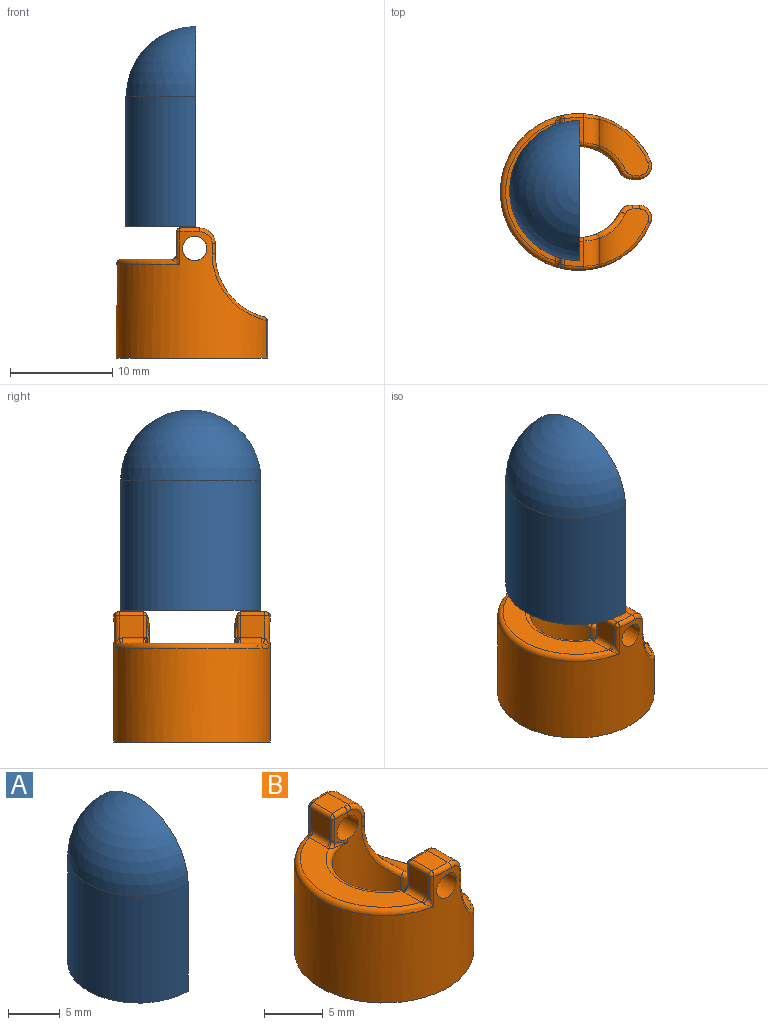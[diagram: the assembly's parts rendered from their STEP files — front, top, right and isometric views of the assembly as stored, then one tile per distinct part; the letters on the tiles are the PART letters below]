
ASSEMBLY  parts=2 mates=1
PART A: 6 faces, bbox 6.8x13.7x19.5 mm
  f0: cylinder r=6.85mm len=13.69mm, axis (0,0,1), area 273.1mm2, adj f1,f4,f5
  f1: plane 13.69x6.85mm, normal (0,0,-1), area 42.6mm2, adj f0,f2,f5
  f2: cylinder r=4.45mm len=12.7mm, axis (0,0,1), area 177.3mm2, adj f1,f3,f5
  f3: sphere r=4.45mm, area 62.1mm2, adj f2,f5
  f4: sphere r=6.85mm, area 147.2mm2, adj f0,f5
  f5: plane 19.55x13.69mm, normal (1,0,0), area 103.5mm2, adj f0,f1,f2,f3,f4
PART B: 72 faces, bbox 15.6x16.2x12.7 mm
  f0: cylinder r=7.64mm len=15.29mm, axis (0,0,-1), area 334.1mm2, adj f4,f5,f7,f9,f17,f19,f27,f29
  f1: cylinder r=4.45mm len=12.32mm, axis (0,0,-1), area 202.2mm2, adj f4,f5,f6,f9,f18,f20,f22,f24
  f2: plane 2.46x1.87mm, normal (0,0,1), area 4.5mm2, adj f7,f13,f28,f57,f59
  f3: plane 2.46x1.87mm, normal (0,0,1), area 4.5mm2, adj f6,f14,f33,f52,f54
  f4: cylinder r=1.2mm len=3.37mm, axis (0,1,0), area 24.1mm2, adj f0,f1,f44
  f5: cylinder r=1.2mm len=3.37mm, axis (0,1,0), area 24.1mm2, adj f0,f1,f43
  f6: torus R=4.83mm, axis (0,0,1), area 0.3mm2, adj f1,f3,f26,f54
  f7: torus R=7.26mm, axis (0,0,1), area 1.2mm2, adj f0,f2,f35,f56
  f8: cylinder r=6.35mm len=6.16mm, axis (0,1,0), area 23.6mm2, adj f11,f21,f22,f23,f25,f27
  f9: plane 15.29x14.76mm, normal (0,0,-1), area 111.7mm2, adj f0,f1,f15,f16,f17,f18,f19,f20
  f10: plane 2.54x1.02mm, normal (1,0,0), area 2.6mm2, adj f12,f13,f32,f37
  f11: plane 2.54x1.02mm, normal (1,0,0), area 2.6mm2, adj f8,f14,f24,f29
  f12: cylinder r=6.35mm len=6.16mm, axis (0,1,0), area 23.6mm2, adj f10,f34,f36,f38,f39,f40
  f13: cylinder r=1.52mm len=2.7mm, axis (0,1,0), area 6mm2, adj f2,f10,f30,f35
  f14: cylinder r=1.52mm len=2.7mm, axis (0,1,0), area 6mm2, adj f3,f11,f26,f31
  f15: plane 4.26x0.73mm, normal (0,1,0), area 3mm2, adj f9,f19,f20,f23
  f16: plane 4.26x0.73mm, normal (0,-1,0), area 3mm2, adj f9,f17,f18,f38
  f17: cylinder r=1.27mm len=3.91mm, axis (0,0,-1), area 9.3mm2, adj f0,f9,f16,f40
  f18: cylinder r=1.27mm len=4.77mm, axis (0,0,-1), area 6.4mm2, adj f1,f9,f16,f36
  f19: cylinder r=1.27mm len=3.91mm, axis (0,0,-1), area 9.3mm2, adj f0,f9,f15,f25
  f20: cylinder r=1.27mm len=4.77mm, axis (0,0,-1), area 6.4mm2, adj f1,f9,f15,f21
  f21: bspline ~1.67x1.39mm, area 1mm2, adj f8,f20,f22,f23
  f22: bspline ~6.16x3.15mm, area 5.1mm2, adj f1,f8,f21,f24
  f23: torus R=6.73mm, axis (0,1,0), area 0.5mm2, adj f8,f15,f21,f25
  f24: cylinder r=0.38mm len=1.02mm, axis (0,0,-1), area 0.7mm2, adj f1,f11,f22,f26
  f25: bspline ~2.03x1.58mm, area 1.2mm2, adj f8,f19,f23,f27
  f26: bspline ~1.89x1.87mm, area 1.5mm2, adj f1,f6,f14,f24
  f27: bspline ~8.01x5.61mm, area 5mm2, adj f0,f8,f25,f29
  f28: torus R=4.83mm, axis (0,0,1), area 0.3mm2, adj f1,f2,f30,f59
  f29: cylinder r=0.38mm len=1.02mm, axis (0,0,-1), area 0.5mm2, adj f0,f11,f27,f31
  f30: bspline ~1.89x1.87mm, area 1.5mm2, adj f1,f13,f28,f32
  f31: bspline ~1.86x1.61mm, area 1.2mm2, adj f0,f14,f29,f33
  f32: cylinder r=0.38mm len=1.02mm, axis (0,0,-1), area 0.7mm2, adj f1,f10,f30,f34
  f33: torus R=7.26mm, axis (0,0,1), area 1.2mm2, adj f0,f3,f31,f51
  f34: bspline ~5.8x3.45mm, area 5.1mm2, adj f1,f12,f32,f36
  f35: bspline ~1.86x1.86mm, area 1.2mm2, adj f0,f7,f13,f37
  f36: bspline ~1.67x1.39mm, area 1mm2, adj f12,f18,f34,f38
  f37: cylinder r=0.38mm len=1.02mm, axis (0,0,-1), area 0.5mm2, adj f0,f10,f35,f39
  f38: torus R=6.73mm, axis (0,1,0), area 0.5mm2, adj f12,f16,f36,f40
  f39: bspline ~6.95x5.61mm, area 5mm2, adj f0,f12,f37,f40
  f40: bspline ~2.03x1.58mm, area 1.2mm2, adj f12,f17,f38,f39
  f41: plane 2.43x2.22mm, normal (-1,0,0), area 5.3mm2, adj f47,f55,f57,f61,f62
  f42: plane 2.43x2.22mm, normal (-1,0,0), area 5.3mm2, adj f46,f50,f52,f67,f68
  f43: plane 3.18x1.53mm, normal (0,1,0), area 2mm2, adj f1,f5,f46,f54,f71
  f44: plane 3.18x1.53mm, normal (0,-1,0), area 2mm2, adj f1,f4,f47,f59,f65
  f45: plane 13.52x4.9mm, normal (0,0,1), area 31.2mm2, adj f48,f49,f62,f63,f68,f69
  f46: cylinder r=0.25mm len=2.47mm, axis (0,0,1), area 0.9mm2, adj f42,f43,f53,f69,f70
  f47: cylinder r=0.25mm len=2.47mm, axis (0,0,1), area 0.9mm2, adj f41,f44,f58,f63,f64
  f48: torus R=7.14mm, axis (0,0,1), area 15.5mm2, adj f0,f45,f60,f61,f66,f67
  f49: torus R=4.95mm, axis (0,0,1), area 9.2mm2, adj f1,f45,f64,f65,f70,f71
  f50: cylinder r=0.38mm len=3.18mm, axis (0,0,-1), area 1.4mm2, adj f0,f42,f51,f66
  f51: sphere r=0.38mm, area 0.2mm2, adj f33,f50,f52
  f52: cylinder r=0.38mm len=2.43mm, axis (0,-1,0), area 1.4mm2, adj f3,f42,f51,f53
  f53: bspline ~0.4x0.38mm, area 0.2mm2, adj f46,f52,f54
  f54: cylinder r=0.38mm len=1.52mm, axis (-1,0,0), area 0.9mm2, adj f3,f6,f43,f53
  f55: cylinder r=0.38mm len=3.18mm, axis (0,0,-1), area 1.4mm2, adj f0,f41,f56,f60
  f56: sphere r=0.38mm, area 0.2mm2, adj f7,f55,f57
  f57: cylinder r=0.38mm len=2.43mm, axis (0,-1,0), area 1.4mm2, adj f2,f41,f56,f58
  f58: bspline ~0.46x0.38mm, area 0.2mm2, adj f47,f57,f59
  f59: cylinder r=0.38mm len=1.52mm, axis (1,0,0), area 0.9mm2, adj f2,f28,f44,f58
  f60: bspline ~1x0.77mm, area 0.4mm2, adj f48,f55,f61
  f61: bspline ~0.68x0.56mm, area 0.2mm2, adj f41,f48,f60,f62
  f62: cylinder r=0.51mm len=2.06mm, axis (0,1,0), area 1.6mm2, adj f41,f45,f61,f63
  f63: torus R=0.76mm, axis (0,0,1), area 0.1mm2, adj f45,f47,f62,f64
  f64: bspline ~0.75x0.68mm, area 0.3mm2, adj f47,f49,f63,f65
  f65: bspline ~2.47x0.96mm, area 0.4mm2, adj f44,f49,f64
  f66: bspline ~1x0.77mm, area 0.4mm2, adj f48,f50,f67
  f67: bspline ~0.84x0.59mm, area 0.2mm2, adj f42,f48,f66,f68
  f68: cylinder r=0.51mm len=2.06mm, axis (0,1,0), area 1.6mm2, adj f42,f45,f67,f69
  f69: torus R=0.76mm, axis (0,0,1), area 0.1mm2, adj f45,f46,f68,f70
  f70: bspline ~0.73x0.67mm, area 0.3mm2, adj f46,f49,f69,f71
  f71: bspline ~2.47x0.96mm, area 0.4mm2, adj f43,f49,f70
PLACE A rot(axis=(0.12,-0.12,-0.99),0deg) t=(-9.93,1.12,16.46)mm
PLACE B t=(-10.03,1.01,3.58)mm fixed
MATE parallel A.f5 <-> B.f11  axis (1,0,0) through (-9.93,-3.32,22.81)mm
